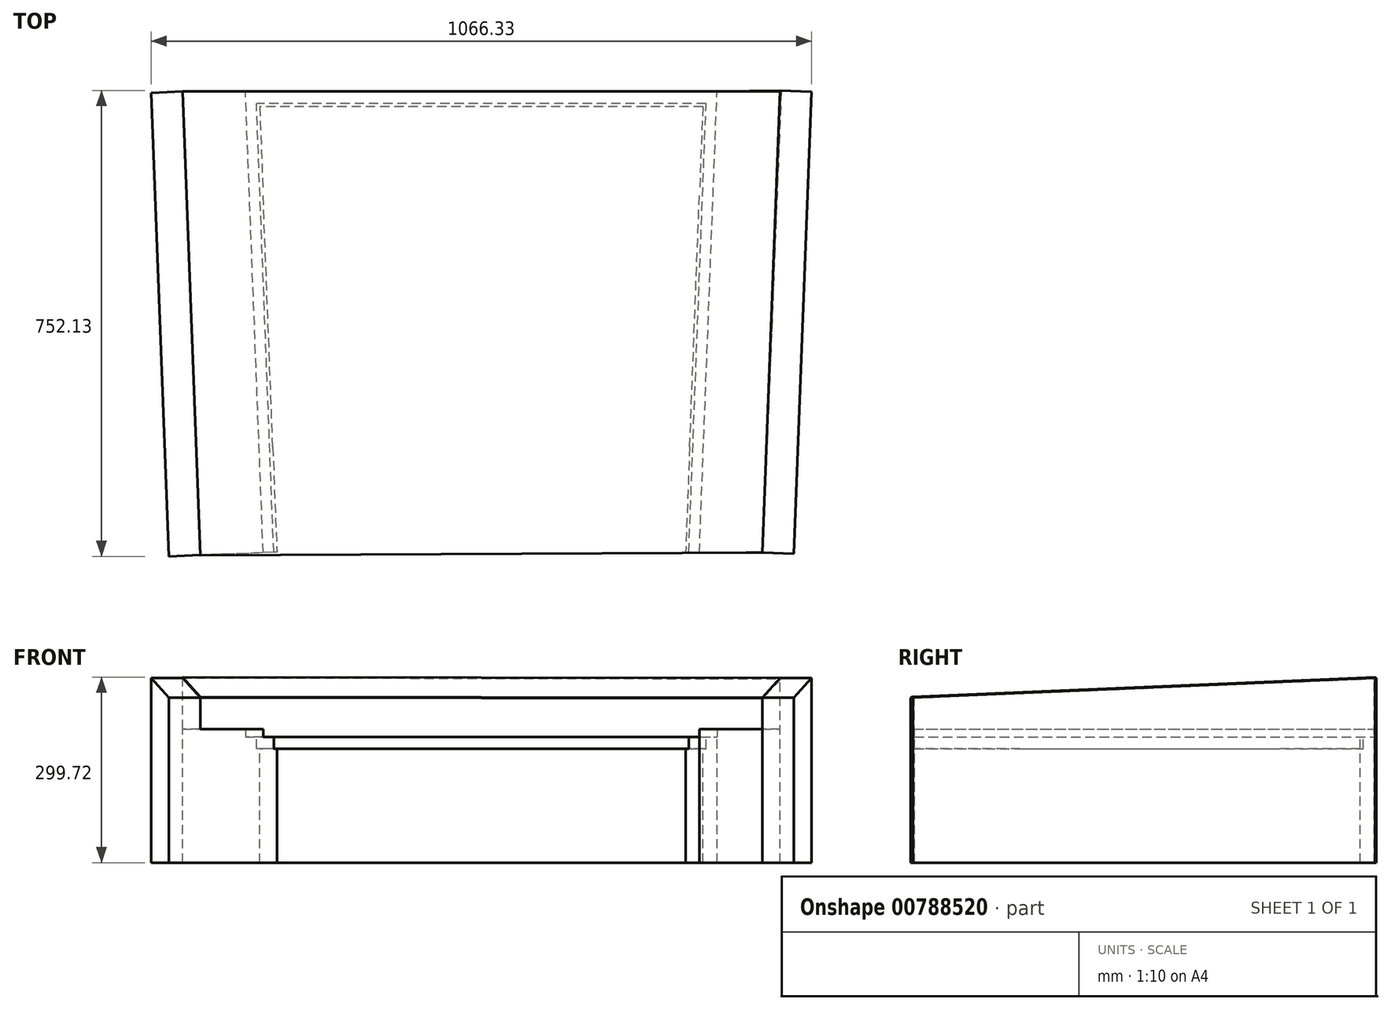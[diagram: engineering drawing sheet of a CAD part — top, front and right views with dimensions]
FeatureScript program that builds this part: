
annotation { "Feature Type Name" : "Feature", "Feature Type Description" : "" }
export const myFeature = defineFeature(function(context is Context, id is Id, definition is map)
    precondition{}
    {
        {
            var Q0;
            Q0=qCreatedBy(makeId("Top.planeOp"),FACE);
            var sketch = newSketch(context, id + "F0", { "sketchPlane" : qUnion([Q0])});
            skLineSegment(sketch, "E0", {"start": v(0, 0) * mm, "end": v(704.85, 0) * mm, "construction": true});
            skLineSegment(sketch, "E1", {"start": v(704.85, 0) * mm, "end": v(704.85, -412.75) * mm, "construction": true});
            skLineSegment(sketch, "E2", {"start": v(704.85, -412.75) * mm, "end": v(688.98, -412.75) * mm, "construction": true});
            skLineSegment(sketch, "E3", {"start": v(0, 0) * mm, "end": v(0, -412.75) * mm, "construction": true});
            skLineSegment(sketch, "E4", {"start": v(0, -412.75) * mm, "end": v(15.88, -412.75) * mm, "construction": true});
            skLineSegment(sketch, "E5", {"start": v(15.88, -412.75) * mm, "end": v(688.98, -412.75) * mm, "construction": true});
            skLineSegment(sketch, "E6", {"start": v(688.98, -412.75) * mm, "end": v(704.85, 0) * mm});
            skLineSegment(sketch, "E7", {"start": v(704.85, 0) * mm, "end": v(884.64, 0) * mm, "construction": true});
            skLineSegment(sketch, "E8", {"start": v(710.1, 136.53) * mm, "end": v(704.85, 136.53) * mm});
            skLineSegment(sketch, "E9", {"start": v(0, 0) * mm, "end": v(352.43, 0) * mm});
            skLineSegment(sketch, "E10", {"start": v(352.43, 0) * mm, "end": v(352.43, -520.69) * mm, "construction": true});
            skLineSegment(sketch, "E11.MirrorCS", {"start": v(15.88, -412.75) * mm, "end": v(0, 0) * mm});
            skLineSegment(sketch, "E12", {"start": v(704.85, 136.53) * mm, "end": v(-5.25, 136.53) * mm});
            skLineSegment(sketch, "E13", {"start": v(710.1, 136.53) * mm, "end": v(704.85, 0) * mm});
            skLineSegment(sketch, "E14", {"start": v(-5.25, 136.53) * mm, "end": v(0, 0) * mm});
            skLineSegment(sketch, "E15", {"start": v(0, -412.75) * mm, "end": v(0, -574.28) * mm, "construction": true});
            skLineSegment(sketch, "E16", {"start": v(15.88, -412.75) * mm, "end": v(22.42, -582.83) * mm});
            skLineSegment(sketch, "E17.MirrorCS", {"start": v(688.98, -412.75) * mm, "end": v(682.43, -582.83) * mm});
            skLineSegment(sketch, "E18", {"start": v(22.42, -582.83) * mm, "end": v(682.43, -582.83) * mm});
            skLineSegment(sketch, "E19", {"start": v(-5.25, 136.53) * mm, "end": v(-10.33, 136.33) * mm});
            skLineSegment(sketch, "E20", {"start": v(22.42, -582.83) * mm, "end": v(17.34, -583.02) * mm});
            skLineSegment(sketch, "E21", {"start": v(17.34, -583.02) * mm, "end": v(-10.33, 136.33) * mm});
            skLineSegment(sketch, "E22.MirrorCS", {"start": v(687.5, -583.02) * mm, "end": v(715.18, 136.33) * mm});
            skLineSegment(sketch, "E23.MirrorCS", {"start": v(710.1, 136.53) * mm, "end": v(715.18, 136.33) * mm});
            skLineSegment(sketch, "E24.MirrorCS", {"start": v(682.43, -582.83) * mm, "end": v(687.5, -583.02) * mm});
            skLineSegment(sketch, "E25", {"start": v(-10.33, 136.33) * mm, "end": v(-27.33, 135.68) * mm});
            skLineSegment(sketch, "E26", {"start": v(17.34, -583.02) * mm, "end": v(0.34, -583.68) * mm});
            skLineSegment(sketch, "E27", {"start": v(0.34, -583.68) * mm, "end": v(-27.33, 135.68) * mm});
            skLineSegment(sketch, "E28.MirrorCS", {"start": v(704.51, -583.68) * mm, "end": v(732.18, 135.68) * mm});
            skLineSegment(sketch, "E29.MirrorCS", {"start": v(715.18, 136.33) * mm, "end": v(732.18, 135.68) * mm});
            skLineSegment(sketch, "E30.MirrorCS", {"start": v(687.5, -583.02) * mm, "end": v(704.51, -583.68) * mm});
            skLineSegment(sketch, "E31", {"start": v(-10.33, 136.33) * mm, "end": v(-10.52, 141.4) * mm});
            skLineSegment(sketch, "E32", {"start": v(715.18, 136.33) * mm, "end": v(715.18, 141.4) * mm});
            skLineSegment(sketch, "E33", {"start": v(715.18, 141.4) * mm, "end": v(-10.52, 141.4) * mm});
            skLineSegment(sketch, "E34", {"start": v(-27.33, 135.68) * mm, "end": v(-28.3, 161.06) * mm});
            skLineSegment(sketch, "E35", {"start": v(732.18, 135.68) * mm, "end": v(733.16, 161.06) * mm});
            skLineSegment(sketch, "E36", {"start": v(733.16, 161.06) * mm, "end": v(-28.3, 161.06) * mm});
            skLineSegment(sketch, "E37", {"start": v(704.51, -583.68) * mm, "end": v(806.11, -583.68) * mm});
            skLineSegment(sketch, "E38", {"start": v(806.11, -583.68) * mm, "end": v(834.82, 162.59) * mm});
            skLineSegment(sketch, "E39", {"start": v(834.82, 162.59) * mm, "end": v(733.16, 161.06) * mm});
            skLineSegment(sketch, "E40", {"start": v(0.34, -583.68) * mm, "end": v(-101.19, -587.58) * mm});
            skLineSegment(sketch, "E41", {"start": v(-101.19, -587.58) * mm, "end": v(-129.98, 161.06) * mm});
            skLineSegment(sketch, "E42", {"start": v(-129.98, 161.06) * mm, "end": v(-28.3, 161.06) * mm});
            skSolve(sketch);
        }
        {
            var Q0;
            Q0=makeQuery(id+"F0.imprint","IMPRINT",FACE,{"disambiguationData":[TD([[makeQuery(id+"F0.imprint","IMPRINT",EDGE,{"derivedFrom":sQuery(id+"F0.wireOp",EDGE,"E27")}),1.0]])]});
            var Q1;
            Q1=makeQuery(id+"F0.imprint","IMPRINT",FACE,{"disambiguationData":[TD([[makeQuery(id+"F0.imprint","IMPRINT",EDGE,{"derivedFrom":sQuery(id+"F0.wireOp",EDGE,"E21")}),1.0]])]});
            var Q2;
            Q2=makeQuery(id+"F0.imprint","IMPRINT",FACE,{"disambiguationData":[TD([[makeQuery(id+"F0.imprint","IMPRINT",EDGE,{"derivedFrom":sQuery(id+"F0.wireOp",EDGE,"E11.MirrorCS")}),1.0]])]});
            var Q3;
            Q3=makeQuery(id+"F0.imprint","IMPRINT",FACE,{"disambiguationData":[TD([[makeQuery(id+"F0.imprint","IMPRINT",EDGE,{"derivedFrom":sQuery(id+"F0.wireOp",EDGE,"E8")}),-1.0]])]});
            var Q4;
            Q4=makeQuery(id+"F0.imprint","IMPRINT",FACE,{"disambiguationData":[TD([[makeQuery(id+"F0.imprint","IMPRINT",EDGE,{"derivedFrom":sQuery(id+"F0.wireOp",EDGE,"E25")}),-1.0]])]});
            var Q5;
            Q5=makeQuery(id+"F0.imprint","IMPRINT",FACE,{"disambiguationData":[TD([[makeQuery(id+"F0.imprint","IMPRINT",EDGE,{"derivedFrom":sQuery(id+"F0.wireOp",EDGE,"E28.MirrorCS")}),-1.0]])]});
            var Q6;
            Q6=makeQuery(id+"F0.imprint","IMPRINT",FACE,{"disambiguationData":[TD([[makeQuery(id+"F0.imprint","IMPRINT",EDGE,{"derivedFrom":sQuery(id+"F0.wireOp",EDGE,"E22.MirrorCS")}),-1.0]])]});
            var Q7;
            Q7=makeQuery(id+"F0.imprint","IMPRINT",FACE,{"disambiguationData":[TD([[makeQuery(id+"F0.imprint","IMPRINT",EDGE,{"derivedFrom":sQuery(id+"F0.wireOp",EDGE,"E6")}),-1.0]])]});
            extrude(context, id + "F1", {"entities" : qUnion([Q0, Q1, Q2, Q3, Q4, Q5, Q6, Q7]), "oppositeDirection" : true, "depth" : 203.2 * mm, "offsetDistance" : 25.4 * mm});
        }
        {
            var Q0;
            Q0=makeQuery(id+"F0.imprint","IMPRINT",FACE,{"disambiguationData":[TD([[makeQuery(id+"F0.imprint","IMPRINT",EDGE,{"derivedFrom":sQuery(id+"F0.wireOp",EDGE,"E27")}),1.0]])]});
            var Q1;
            Q1=makeQuery(id+"F0.imprint","IMPRINT",FACE,{"disambiguationData":[TD([[makeQuery(id+"F0.imprint","IMPRINT",EDGE,{"derivedFrom":sQuery(id+"F0.wireOp",EDGE,"E28.MirrorCS")}),-1.0]])]});
            extrude(context, id + "F2", {"entities" : qUnion([Q0, Q1]), "operationType" : NewBodyOperationType.ADD, "depth" : 12.7 * mm, "offsetDistance" : 25.4 * mm});
        }
        {
            var Q0;
            Q0=makeQuery(id+"F0.imprint","IMPRINT",FACE,{"disambiguationData":[TD([[makeQuery(id+"F0.imprint","IMPRINT",EDGE,{"derivedFrom":sQuery(id+"F0.wireOp",EDGE,"E11.MirrorCS")}),1.0]])]});
            var Q1;
            Q1=makeQuery(id+"F0.imprint","IMPRINT",FACE,{"disambiguationData":[TD([[makeQuery(id+"F0.imprint","IMPRINT",EDGE,{"derivedFrom":sQuery(id+"F0.wireOp",EDGE,"E6")}),-1.0]])]});
            var Q2;
            Q2=makeQuery(id+"F0.imprint","IMPRINT",FACE,{"disambiguationData":[TD([[makeQuery(id+"F0.imprint","IMPRINT",EDGE,{"derivedFrom":sQuery(id+"F0.wireOp",EDGE,"E8")}),-1.0]])]});
            extrude(context, id + "F3", {"entities" : qUnion([Q0, Q1, Q2]), "operationType" : NewBodyOperationType.REMOVE, "oppositeDirection" : true, "depth" : 19.05 * mm, "offsetDistance" : 25.4 * mm});
        }
        {
            var Q0;
            {var subQ0=sQuery(id+"F0.wireOp",EDGE,"E38");Q0=makeQuery(id+"F2.boolean.opBoolean","MERGE",FACE,{"derivedFrom":[makeQuery(id+"F1.opExtrude","SWEPT_FACE",FACE,{"disambiguationData":[OSD([subQ0])]}),makeQuery(id+"F2.opExtrude","SWEPT_FACE",FACE,{"disambiguationData":[OSD([subQ0])]})]});}
            var sketch = newSketch(context, id + "F4", { "sketchPlane" : qUnion([Q0])});
            skLineSegment(sketch, "E43", {"start": v(-552.26, 12.7) * mm, "end": v(-552.26, 63.5) * mm});
            skLineSegment(sketch, "E44", {"start": v(194.56, 12.7) * mm, "end": v(194.56, 95.25) * mm});
            skLineSegment(sketch, "E45", {"start": v(194.56, 95.25) * mm, "end": v(-552.26, 63.5) * mm});
            skLineSegment(sketch, "E46", {"start": v(-552.26, 12.7) * mm, "end": v(-552.26, -203.2) * mm});
            skLineSegment(sketch, "E47", {"start": v(-552.26, -203.2) * mm, "end": v(194.56, -203.2) * mm});
            skLineSegment(sketch, "E48", {"start": v(194.56, -203.2) * mm, "end": v(194.56, 12.7) * mm});
            skSolve(sketch);
        }
        {
            var Q0;
            Q0=makeQuery(id+"F4.imprint","IMPRINT",FACE,{"disambiguationData":[TD([[makeQuery(id+"F4.imprint","IMPRINT",EDGE,{"derivedFrom":sQuery(id+"F4.wireOp",EDGE,"E43")}),-1.0]])]});
            var Q1;
            Q1=makeQuery(id+"F4.imprint","IMPRINT",FACE,{"disambiguationData":[TD([[makeQuery(id+"F4.imprint","IMPRINT",EDGE,{"derivedFrom":sQuery(id+"F4.wireOp",EDGE,"E46")}),-1.0]])]});
            extrude(context, id + "F5", {"entities" : qUnion([Q0, Q1]), "depth" : 50.8 * mm, "offsetDistance" : 25.4 * mm});
        }
        {
            var Q0;
            {var subQ0=sQuery(id+"F0.wireOp",EDGE,"E41");Q0=makeQuery(id+"F2.boolean.opBoolean","MERGE",FACE,{"derivedFrom":[makeQuery(id+"F1.opExtrude","SWEPT_FACE",FACE,{"disambiguationData":[OSD([subQ0])]}),makeQuery(id+"F2.opExtrude","SWEPT_FACE",FACE,{"disambiguationData":[OSD([subQ0])]})]});}
            var sketch = newSketch(context, id + "F6", { "sketchPlane" : qUnion([Q0])});
            skLineSegment(sketch, "E49", {"start": v(-165.93, 12.7) * mm, "end": v(-165.93, 95.25) * mm});
            skLineSegment(sketch, "E50", {"start": v(583.26, 12.7) * mm, "end": v(583.26, 63.5) * mm});
            skLineSegment(sketch, "E51", {"start": v(583.26, 63.5) * mm, "end": v(-165.93, 95.25) * mm});
            skLineSegment(sketch, "E52", {"start": v(-165.93, 12.7) * mm, "end": v(-165.93, -203.2) * mm});
            skLineSegment(sketch, "E53", {"start": v(-165.93, -203.2) * mm, "end": v(583.26, -203.2) * mm});
            skLineSegment(sketch, "E54", {"start": v(583.26, -203.2) * mm, "end": v(583.26, 12.7) * mm});
            skSolve(sketch);
        }
        {
            var Q0;
            Q0 = qSketchRegion(id + "F6", true);
            extrude(context, id + "F7", {"entities" : qUnion([Q0]), "operationType" : NewBodyOperationType.ADD, "depth" : 50.8 * mm, "offsetDistance" : 25.4 * mm});
        }
        {
            var Q0;
            Q0=makeQuery(id+"F7.opExtrude","SWEPT_FACE",FACE,{"disambiguationData":[OSD([sQuery(id+"F6.wireOp",EDGE,"E51")])]});
            var sketch = newSketch(context, id + "F8", { "sketchPlane" : qUnion([Q0])});
            skLineSegment(sketch, "E55", {"start": v(-130.13, 164.94) * mm, "end": v(836.66, 164.94) * mm});
            skLineSegment(sketch, "E56", {"start": v(836.66, 164.94) * mm, "end": v(806.41, -580.35) * mm});
            skLineSegment(sketch, "E57", {"start": v(806.41, -580.35) * mm, "end": v(-101.33, -584.37) * mm});
            skLineSegment(sketch, "E58", {"start": v(-101.33, -584.37) * mm, "end": v(-130.13, 164.94) * mm});
            skSolve(sketch);
        }
        {
            var Q0;
            Q0=makeQuery(id+"F8.imprint","IMPRINT",FACE,{"disambiguationData":[TD([[makeQuery(id+"F8.imprint","IMPRINT",EDGE,{"derivedFrom":sQuery(id+"F8.wireOp",EDGE,"E55")}),-1.0]])]});
            extrude(context, id + "F9", {"entities" : qUnion([Q0]), "depth" : 1.27 * mm, "offsetDistance" : 25.4 * mm});
        }
    });
